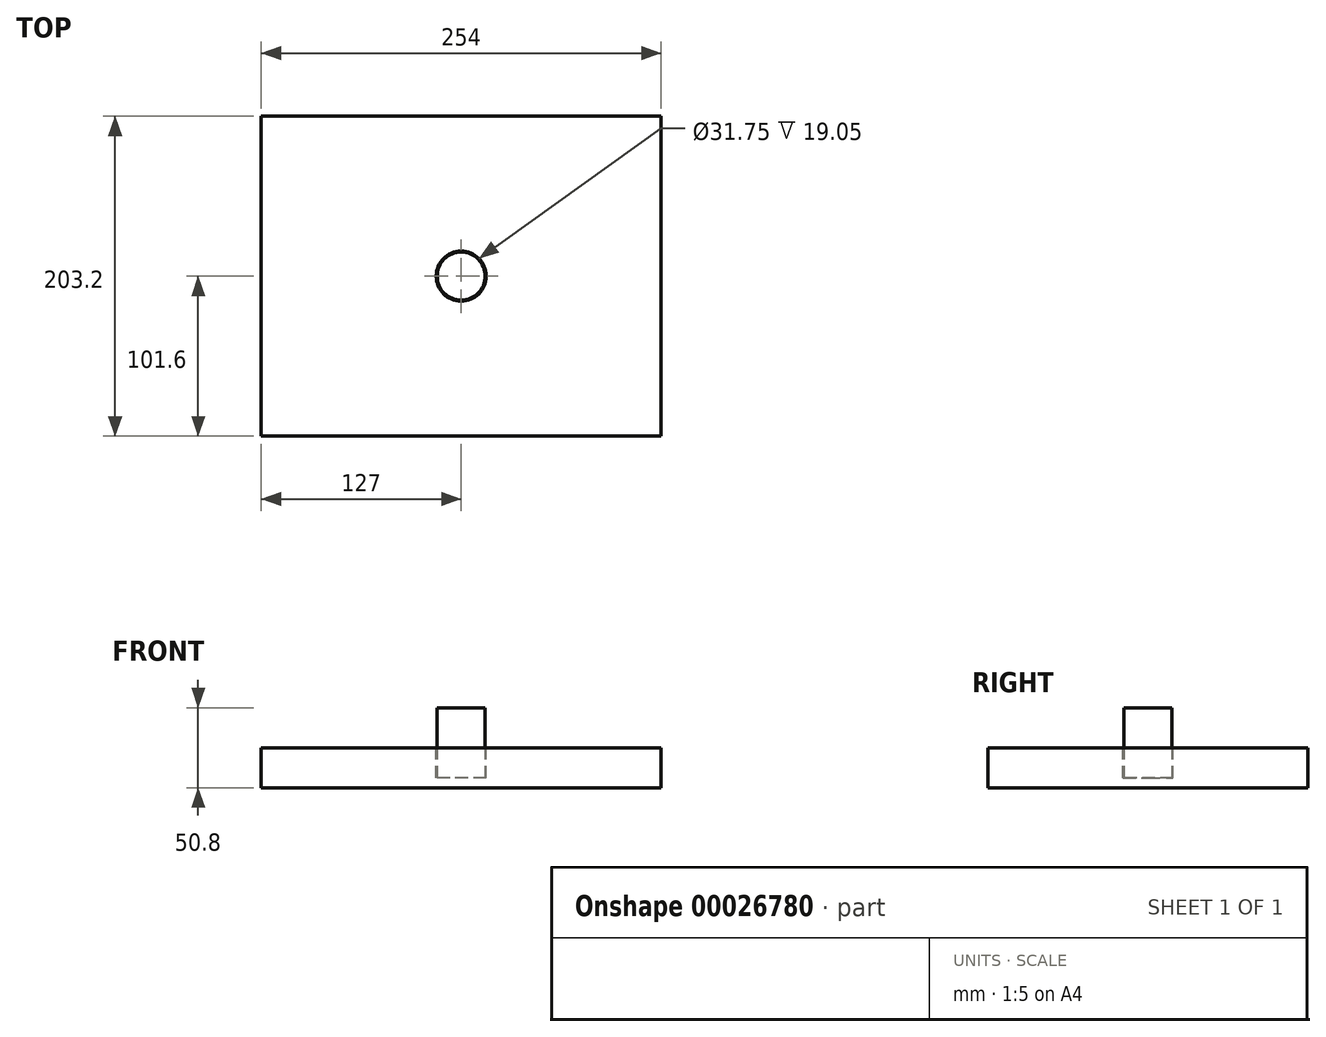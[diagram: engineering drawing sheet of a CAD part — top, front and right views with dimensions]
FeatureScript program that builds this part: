
annotation { "Feature Type Name" : "Feature", "Feature Type Description" : "" }
export const myFeature = defineFeature(function(context is Context, id is Id, definition is map)
    precondition{}
    {
        {
            var Q0;
            Q0=qCreatedBy(makeId("Top.planeOp"),FACE);
            var sketch = newSketch(context, id + "F0", { "sketchPlane" : qUnion([Q0])});
            skLineSegment(sketch, "E0.rect.bottom", {"start": v(127, -101.6) * mm, "end": v(-127, -101.6) * mm});
            skLineSegment(sketch, "E0.rect.top", {"start": v(127, 101.6) * mm, "end": v(-127, 101.6) * mm});
            skLineSegment(sketch, "E0.rect.left", {"start": v(127, -101.6) * mm, "end": v(127, 101.6) * mm});
            skLineSegment(sketch, "E0.rect.right", {"start": v(-127, -101.6) * mm, "end": v(-127, 101.6) * mm});
            skPoint(sketch, "E0.rect.middle", {"position": v(0, 0) * mm});
            skSolve(sketch);
        }
        {
            var Q0;
            Q0=makeQuery(id+"F0.imprint","IMPRINT",FACE,{"disambiguationData":[TD([[makeQuery(id+"F0.imprint","IMPRINT",EDGE,{"derivedFrom":sQuery(id+"F0.wireOp",EDGE,"E0.rect.bottom")}),-1.0]])]});
            extrude(context, id + "F1", {"entities" : qUnion([Q0]), "depth" : 25.4 * mm});
        }
        {
            var Q0;
            Q0=makeQuery(id+"F1.opExtrude","CAP_FACE",FACE,{"disambiguationData":[OSD([sQuery(id+"F0.wireOp",EDGE,"E0.rect.bottom"),sQuery(id+"F0.wireOp",EDGE,"E0.rect.top"),sQuery(id+"F0.wireOp",EDGE,"E0.rect.left"),sQuery(id+"F0.wireOp",EDGE,"E0.rect.right")])],"isStart":false});
            var sketch = newSketch(context, id + "F2", { "sketchPlane" : qUnion([Q0])});
            skCircle(sketch, "E1", {"center": v(0, 0) * mm, "radius": 15.88 * mm});
            skSolve(sketch);
        }
        {
            var Q0;
            Q0 = qSketchRegion(id + "F2", true);
            extrude(context, id + "F3", {"entities" : qUnion([Q0]), "operationType" : NewBodyOperationType.REMOVE, "oppositeDirection" : true, "depth" : 19.05 * mm});
        }
        {
            var Q0;
            Q0=makeQuery(id+"F3.boolean.opBoolean","COPY",FACE,{"derivedFrom":makeQuery(id+"F3.opExtrude","CAP_FACE",FACE,{"disambiguationData":[OSD([sQuery(id+"F2.wireOp",EDGE,"E1")])],"isStart":false})});
            var sketch = newSketch(context, id + "F4", { "sketchPlane" : qUnion([Q0])});
            skCircle(sketch, "E2", {"center": v(0, 0) * mm, "radius": 15.24 * mm});
            skSolve(sketch);
        }
        {
            var Q0;
            Q0 = qSketchRegion(id + "F4", true);
            extrude(context, id + "F5", {"entities" : qUnion([Q0]), "depth" : 44.45 * mm});
        }
    });
